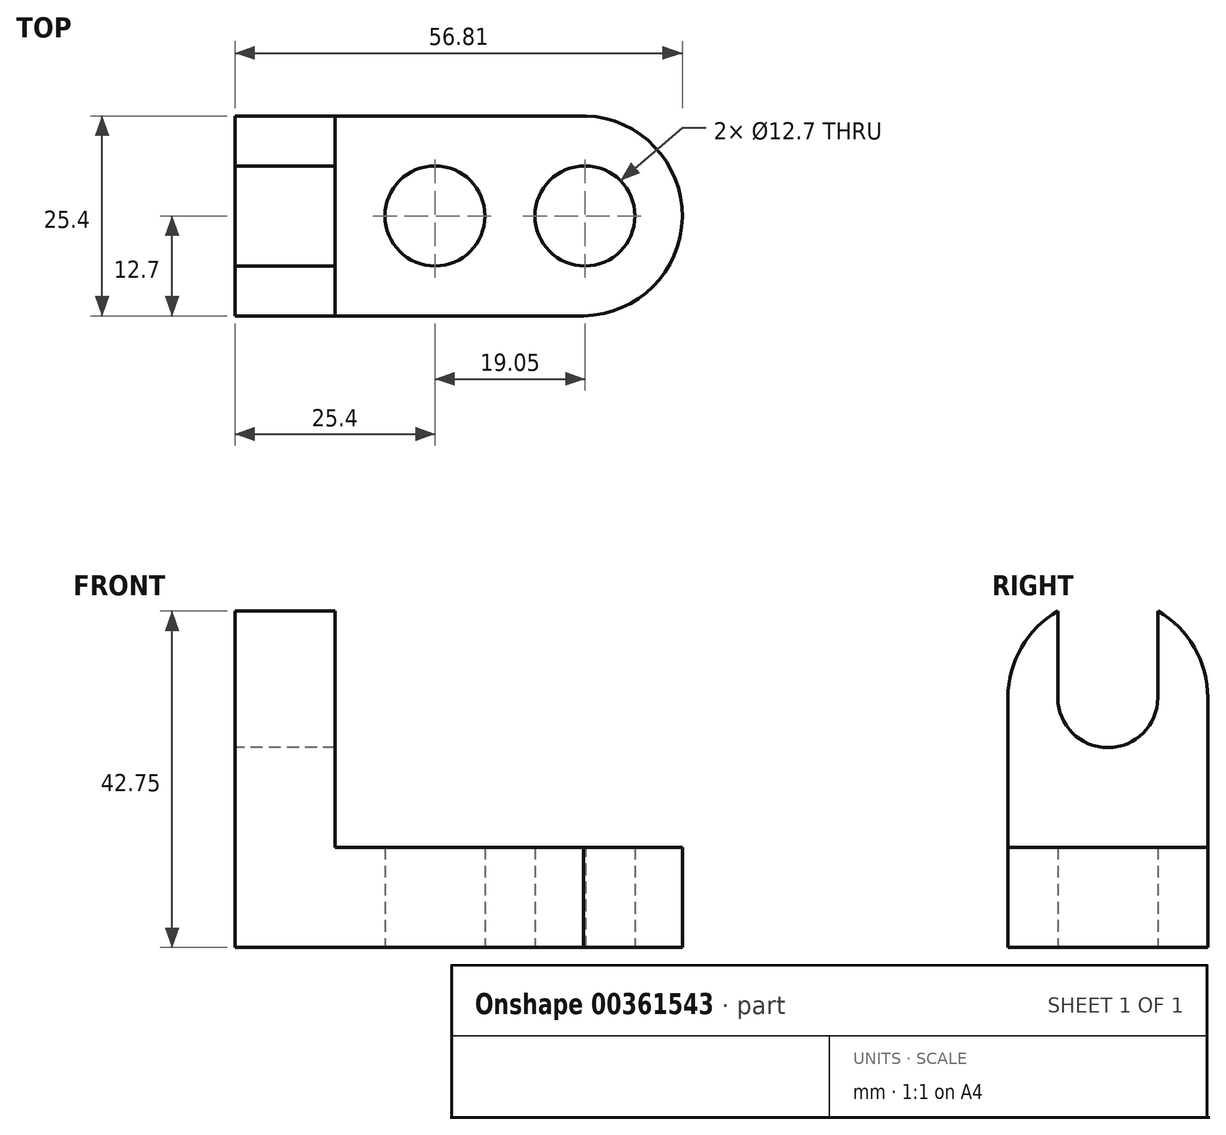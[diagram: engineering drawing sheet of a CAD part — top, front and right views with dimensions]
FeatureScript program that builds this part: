
annotation { "Feature Type Name" : "Feature", "Feature Type Description" : "" }
export const myFeature = defineFeature(function(context is Context, id is Id, definition is map)
    precondition{}
    {
        {
            var Q0;
            Q0=qCreatedBy(makeId("Top.planeOp"),FACE);
            var sketch = newSketch(context, id + "F0", { "sketchPlane" : qUnion([Q0])});
            skLineSegment(sketch, "E0", {"start": v(0, 25.4) * mm, "end": v(44.45, 25.4) * mm});
            skLineSegment(sketch, "E1", {"start": v(44.45, 25.4) * mm, "end": v(44.45, 0) * mm});
            skLineSegment(sketch, "E2", {"start": v(44.45, 0) * mm, "end": v(0, 0) * mm});
            skLineSegment(sketch, "E3", {"start": v(0, 0) * mm, "end": v(0, 25.4) * mm});
            skCircle(sketch, "E4", {"center": v(31.75, 12.7) * mm, "radius": 6.35 * mm});
            skCircle(sketch, "E5", {"center": v(12.7, 12.7) * mm, "radius": 6.35 * mm});
            skArc(sketch, "E6", {"start": v(31.75, 0) * mm, "mid": v(44.3, 12.7) * mm, "end": v(31.75, 25.4) * mm});
            skSolve(sketch);
        }
        {
            var Q0;
            Q0 = qSketchRegion(id + "F0", true);
            extrude(context, id + "F1", {"entities" : qUnion([Q0]), "depth" : 12.7 * mm});
        }
        {
            var Q0;
            Q0=makeQuery(id+"F1.opExtrude","CAP_FACE",FACE,{"disambiguationData":[OSD([sQuery(id+"F0.wireOp",EDGE,"E0"),sQuery(id+"F0.wireOp",EDGE,"E1"),sQuery(id+"F0.wireOp",EDGE,"E2"),sQuery(id+"F0.wireOp",EDGE,"E3"),sQuery(id+"F0.wireOp",EDGE,"E4"),sQuery(id+"F0.wireOp",EDGE,"E5")])],"isStart":false});
            var sketch = newSketch(context, id + "F2", { "sketchPlane" : qUnion([Q0])});
            skArc(sketch, "E7", {"start": v(31.26, 0) * mm, "mid": v(44.11, 12.86) * mm, "end": v(30.95, 25.4) * mm});
            skSolve(sketch);
        }
        {
            var Q0;
            {var subQ5=makeQuery(id+"F1.opExtrude","CAP_EDGE",EDGE,{"disambiguationData":[OSD([sQuery(id+"F0.wireOp",EDGE,"E1")])],"isStart":false});Q0=makeQuery(id+"F2.imprint","IMPRINT",FACE,{"disambiguationData":[TD([[makeQuery(id+"F2.imprint","IMPRINT",EDGE,{"derivedFrom":subQ5}),-1.0]])]});}
            extrude(context, id + "F3", {"entities" : qUnion([Q0]), "operationType" : NewBodyOperationType.REMOVE, "oppositeDirection" : true, "depth" : 12.7 * mm});
        }
        {
            var Q0;
            Q0=makeQuery(id+"F1.opExtrude","SWEPT_FACE",FACE,{"disambiguationData":[OSD([sQuery(id+"F0.wireOp",EDGE,"E3")])]});
            var sketch = newSketch(context, id + "F4", { "sketchPlane" : qUnion([Q0])});
            skLineSegment(sketch, "E8", {"start": v(-25.4, 0) * mm, "end": v(-25.4, 44.45) * mm});
            skLineSegment(sketch, "E9", {"start": v(-25.4, 44.45) * mm, "end": v(0, 44.45) * mm});
            skLineSegment(sketch, "E10", {"start": v(0, 0) * mm, "end": v(0, 44.45) * mm});
            skLineSegment(sketch, "E11", {"start": v(-25.4, 0) * mm, "end": v(0, 0) * mm});
            skSolve(sketch);
        }
        {
            var Q0;
            {var subQ2=sQuery(id+"F4.wireOp",EDGE,"E9");Q0=makeQuery(id+"F4.imprint","IMPRINT",FACE,{"disambiguationData":[TD([[makeQuery(id+"F4.imprint","IMPRINT",EDGE,{"derivedFrom":subQ2}),-1.0]])]});}
            var Q1;
            {var subQ0=sQuery(id+"F4.wireOp",EDGE,"E11");Q1=makeQuery(id+"F4.imprint","IMPRINT",FACE,{"disambiguationData":[TD([[makeQuery(id+"F4.imprint","IMPRINT",EDGE,{"derivedFrom":subQ0}),-1.0]])]});}
            extrude(context, id + "F5", {"entities" : qUnion([Q0, Q1]), "operationType" : NewBodyOperationType.ADD, "depth" : 12.7 * mm});
        }
        {
            var Q0;
            Q0=makeQuery(id+"F5.opExtrude","CAP_FACE",FACE,{"disambiguationData":[OSD([sQuery(id+"F4.wireOp",EDGE,"E8"),sQuery(id+"F4.wireOp",EDGE,"E9"),sQuery(id+"F4.wireOp",EDGE,"E10"),sQuery(id+"F4.wireOp",EDGE,"E11")])],"isStart":false});
            var sketch = newSketch(context, id + "F6", { "sketchPlane" : qUnion([Q0])});
            skLineSegment(sketch, "E12", {"start": v(-19.05, 44.45) * mm, "end": v(-19.05, 31.75) * mm});
            skLineSegment(sketch, "E13", {"start": v(-6.35, 44.45) * mm, "end": v(-6.35, 31.75) * mm});
            skArc(sketch, "E14", {"start": v(-19.05, 31.75) * mm, "mid": v(-12.7, 25.4) * mm, "end": v(-6.35, 31.75) * mm});
            skSolve(sketch);
        }
        {
            var Q0;
            {var subQ0=sQuery(id+"F6.wireOp",EDGE,"E12");Q0=makeQuery(id+"F6.imprint","IMPRINT",FACE,{"disambiguationData":[TD([[makeQuery(id+"F6.imprint","IMPRINT",EDGE,{"derivedFrom":subQ0}),1.0]])]});}
            extrude(context, id + "F7", {"entities" : qUnion([Q0]), "operationType" : NewBodyOperationType.REMOVE, "oppositeDirection" : true, "depth" : 12.7 * mm});
        }
        {
            var Q0;
            Q0=makeQuery(id+"F5.opExtrude","CAP_FACE",FACE,{"disambiguationData":[OSD([sQuery(id+"F4.wireOp",EDGE,"E8"),sQuery(id+"F4.wireOp",EDGE,"E9"),sQuery(id+"F4.wireOp",EDGE,"E10"),sQuery(id+"F4.wireOp",EDGE,"E11")])],"isStart":false});
            var sketch = newSketch(context, id + "F8", { "sketchPlane" : qUnion([Q0])});
            skArc(sketch, "E15", {"start": v(0, 31.75) * mm, "mid": v(-12.7, 44.45) * mm, "end": v(-25.4, 31.75) * mm});
            skSolve(sketch);
        }
        {
            var Q0;
            {var subQ0=sQuery(id+"F8.wireOp",EDGE,"E15");var subQ1=sQuery(id+"F4.wireOp",EDGE,"E8");var subQ2=makeQuery(id+"F5.opExtrude","CAP_EDGE",EDGE,{"disambiguationData":[OSD([subQ1])],"isStart":false});var subQ3=makeQuery(id+"F8.imprint","INTERSECT",VERTEX,{"derivedFrom":[subQ2,subQ0]});Q0=makeQuery(id+"F8.imprint","IMPRINT",FACE,{"disambiguationData":[TD([[makeQuery(id+"F8.imprint","IMPRINT",EDGE,{"disambiguationData":[TD([[subQ3,1.0]])],"derivedFrom":subQ0}),-1.0]])]});}
            var Q1;
            {var subQ0=sQuery(id+"F8.wireOp",EDGE,"E15");var subQ1=sQuery(id+"F4.wireOp",EDGE,"E10");var subQ2=makeQuery(id+"F5.opExtrude","CAP_EDGE",EDGE,{"disambiguationData":[OSD([subQ1])],"isStart":false});var subQ3=makeQuery(id+"F8.imprint","INTERSECT",VERTEX,{"derivedFrom":[subQ2,subQ0]});Q1=makeQuery(id+"F8.imprint","IMPRINT",FACE,{"disambiguationData":[TD([[makeQuery(id+"F8.imprint","IMPRINT",EDGE,{"disambiguationData":[TD([[subQ3,-1.0]])],"derivedFrom":subQ0}),-1.0]])]});}
            extrude(context, id + "F9", {"entities" : qUnion([Q0, Q1]), "operationType" : NewBodyOperationType.REMOVE, "oppositeDirection" : true, "depth" : 12.7 * mm});
        }
    });
